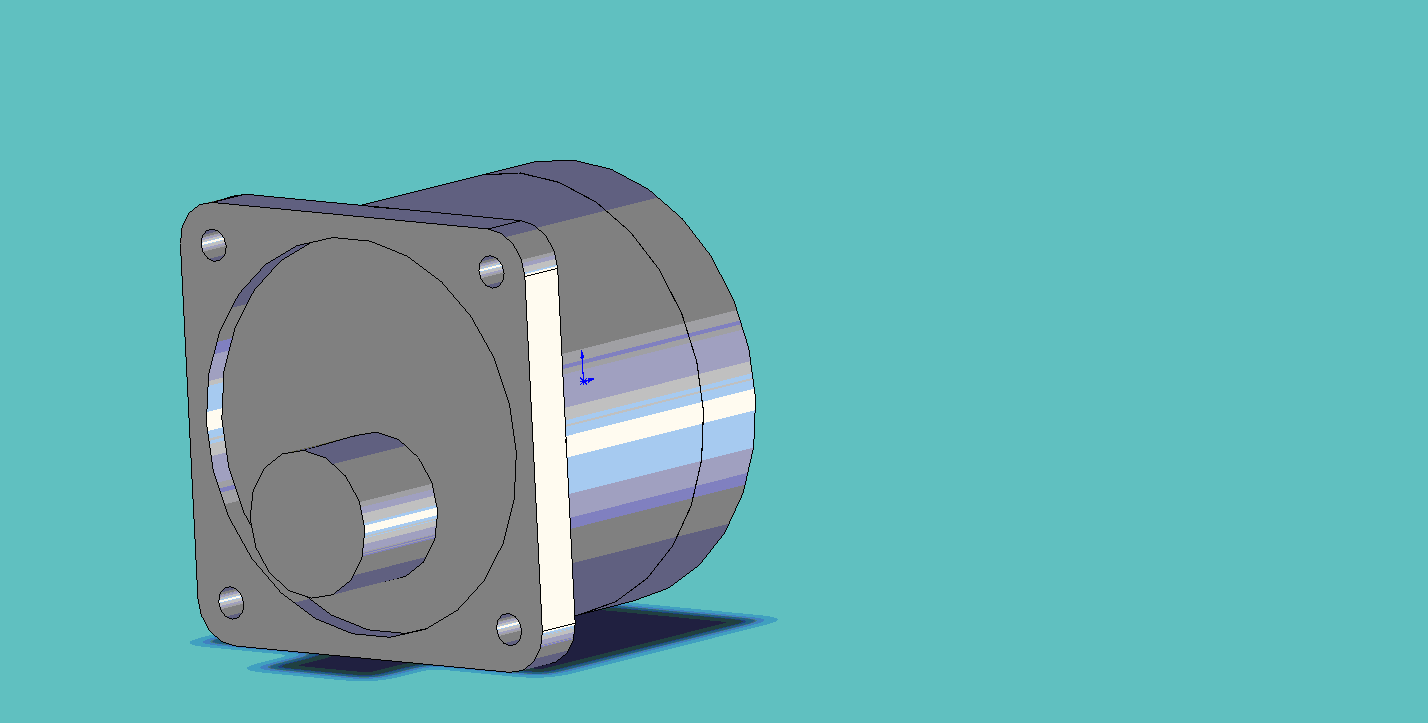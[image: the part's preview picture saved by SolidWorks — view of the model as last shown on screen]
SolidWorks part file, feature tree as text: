
SOLIDWORKS PART (.sldprt)
format: sldprt  version: not decoded by parser v0  size: 189,952 bytes
history: native  units: mm
features: sketch x5, plane x3, cut_extrude x2, material x1, revolve x1, extrude x1, fillet x1, cut_revolve x1 (+8 scaffold rows collapsed)
feature tree (23):
  scaffold x8  (default folders/planes/origin — collapsed)
  material  "Matériau <non spécifié>"
  plane  "Plan de face"
  plane  "Plan de dessus"
  plane  "Plan de droite"
  sketch  "Esquisse1"  dims[D1=30.0mm D2=29.98mm D3=5.4mm D4=19.6mm]
  revolve  "Révolution1"  Angle=360deg
  sketch  "Esquisse2"  dims[c1.D6=2.2mm c1.D2=30.0mm c1.D3=15.0mm c1.D4=15.0mm c1.D1=24.2mm c1.D5=30.0mm c2.D1=3.0mm]
  extrude  "Extrusion1"  Depth=3.4mm
  sketch  "Esquisse3"  dims[D1=27.0mm]
  cut_extrude  "Enlèv. mat.-Extru.1"  Depth=1.6mm
  fillet  "Congé1"  Radius=3mm
  sketch  "Esquisse4"  dims[D2=10.0mm D1=4.9mm]
  cut_extrude  "Extrusion2"  Depth=7.55mm
  sketch  "Esquisse5"  dims[D1=3.0mm D2=1.1mm D3=8.5mm D4=2.0mm D5=4.2mm D6=8.0mm]
  cut_revolve  "Enlèvement de matière-Révolution1"  Angle=360deg
decode coverage: 11 of 11 modeling features carry decoded parameters
note: suppression state not decoded; provenance and decode notes live in map.json
